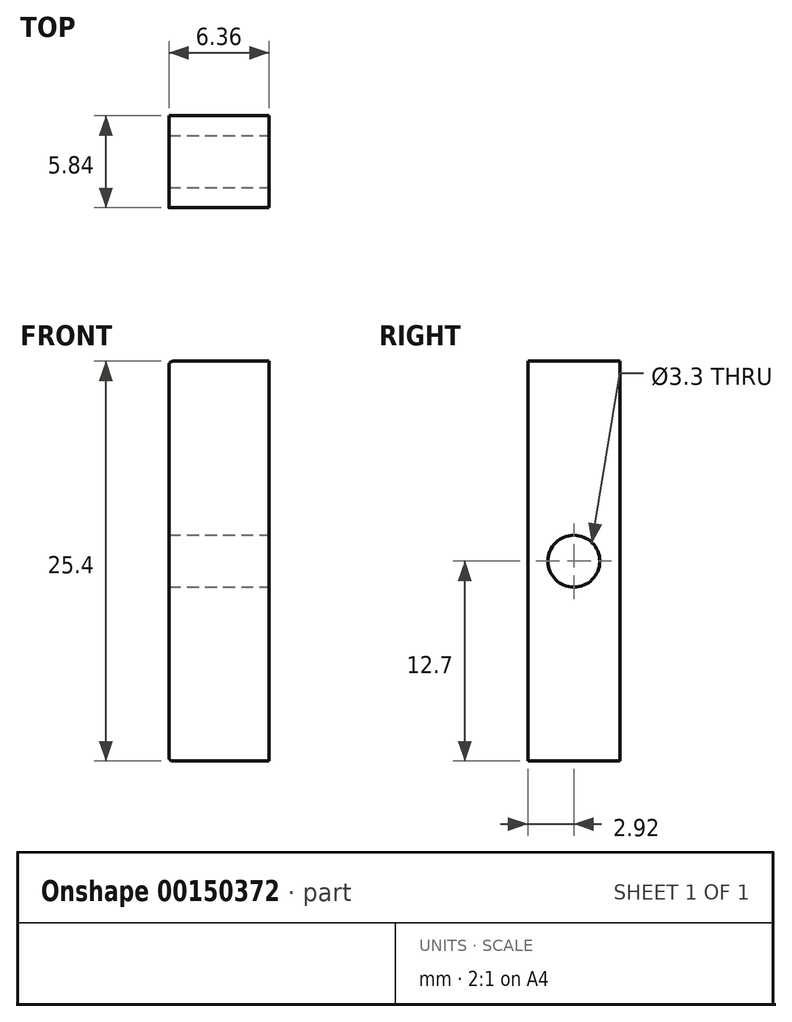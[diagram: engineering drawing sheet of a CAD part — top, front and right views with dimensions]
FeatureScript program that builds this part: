
annotation { "Feature Type Name" : "Feature", "Feature Type Description" : "" }
export const myFeature = defineFeature(function(context is Context, id is Id, definition is map)
    precondition{}
    {
        {
            var Q0;
            Q0=qCreatedBy(makeId("Front.planeOp"),FACE);
            var sketch = newSketch(context, id + "F0", { "sketchPlane" : qUnion([Q0])});
            skLineSegment(sketch, "E0.bottom", {"start": v(4.45, 12.7) * mm, "end": v(-4.45, 12.7) * mm});
            skLineSegment(sketch, "E0.top", {"start": v(4.45, -12.7) * mm, "end": v(-4.45, -12.7) * mm});
            skLineSegment(sketch, "E0.left", {"start": v(4.45, 12.7) * mm, "end": v(4.45, -12.7) * mm});
            skPoint(sketch, "E0.middle", {"position": v(0, 0) * mm});
            skArc(sketch, "E1", {"start": v(-4.45, 11.38) * mm, "mid": v(-3.78, 12.04) * mm, "end": v(-4.45, 12.7) * mm});
            skLineSegment(sketch, "E2", {"start": v(-4.44, 11.38) * mm, "end": v(-4.44, 10.54) * mm});
            skLineSegment(sketch, "E3", {"start": v(-4.45, 12.7) * mm, "end": v(-4.45, 11.38) * mm, "construction": true});
            skArc(sketch, "E4.1.0.0", {"start": v(-4.45, 9.37) * mm, "mid": v(-3.78, 10.03) * mm, "end": v(-4.45, 10.7) * mm});
            skLineSegment(sketch, "E4.1.0.1", {"start": v(-4.45, 9.37) * mm, "end": v(-4.45, 8.53) * mm});
            skArc(sketch, "E4.2.0.0", {"start": v(-4.45, 7.37) * mm, "mid": v(-3.78, 8.03) * mm, "end": v(-4.45, 8.69) * mm});
            skLineSegment(sketch, "E4.2.0.1", {"start": v(-4.45, 7.37) * mm, "end": v(-4.45, 6.53) * mm});
            skArc(sketch, "E4.3.0.0", {"start": v(-4.45, 5.36) * mm, "mid": v(-3.78, 6.02) * mm, "end": v(-4.45, 6.68) * mm});
            skLineSegment(sketch, "E4.3.0.1", {"start": v(-4.45, 5.36) * mm, "end": v(-4.45, 4.52) * mm});
            skArc(sketch, "E4.4.0.0", {"start": v(-4.45, 3.35) * mm, "mid": v(-3.78, 4.01) * mm, "end": v(-4.45, 4.67) * mm});
            skLineSegment(sketch, "E4.4.0.1", {"start": v(-4.45, 3.35) * mm, "end": v(-4.45, 2.51) * mm});
            skArc(sketch, "E4.5.0.0", {"start": v(-4.45, 1.35) * mm, "mid": v(-3.78, 2) * mm, "end": v(-4.45, 2.67) * mm});
            skLineSegment(sketch, "E4.5.0.1", {"start": v(-4.45, 1.35) * mm, "end": v(-4.45, 0.5) * mm});
            skArc(sketch, "E4.6.0.0", {"start": v(-4.45, -0.66) * mm, "mid": v(-3.78, 0) * mm, "end": v(-4.45, 0.66) * mm});
            skLineSegment(sketch, "E4.6.0.1", {"start": v(-4.44, -0.66) * mm, "end": v(-4.44, -1.5) * mm});
            skArc(sketch, "E4.7.0.0", {"start": v(-4.45, -2.67) * mm, "mid": v(-3.78, -2) * mm, "end": v(-4.45, -1.35) * mm});
            skLineSegment(sketch, "E4.7.0.1", {"start": v(-4.44, -2.67) * mm, "end": v(-4.44, -3.5) * mm});
            skArc(sketch, "E4.8.0.0", {"start": v(-4.45, -4.67) * mm, "mid": v(-3.78, -4.01) * mm, "end": v(-4.45, -3.35) * mm});
            skLineSegment(sketch, "E4.8.0.1", {"start": v(-4.44, -4.67) * mm, "end": v(-4.44, -5.51) * mm});
            skArc(sketch, "E4.9.0.0", {"start": v(-4.45, -6.68) * mm, "mid": v(-3.78, -6.02) * mm, "end": v(-4.45, -5.36) * mm});
            skLineSegment(sketch, "E4.9.0.1", {"start": v(-4.44, -6.68) * mm, "end": v(-4.44, -7.52) * mm});
            skArc(sketch, "E4.10.0.0", {"start": v(-4.45, -8.69) * mm, "mid": v(-3.78, -8.03) * mm, "end": v(-4.45, -7.37) * mm});
            skLineSegment(sketch, "E4.10.0.1", {"start": v(-4.44, -8.69) * mm, "end": v(-4.44, -9.53) * mm});
            skArc(sketch, "E4.11.0.0", {"start": v(-4.45, -10.7) * mm, "mid": v(-3.78, -10.03) * mm, "end": v(-4.45, -9.37) * mm});
            skLineSegment(sketch, "E4.11.0.1", {"start": v(-4.44, -10.7) * mm, "end": v(-4.44, -11.53) * mm});
            skArc(sketch, "E4.12.0.0", {"start": v(-4.45, -12.7) * mm, "mid": v(-3.78, -12.04) * mm, "end": v(-4.45, -11.38) * mm});
            skLineSegment(sketch, "E4.direction1", {"start": v(-4.45, 11.38) * mm, "end": v(-4.45, 9.37) * mm, "construction": true});
            skLineSegment(sketch, "E5", {"start": v(-4.45, 12.7) * mm, "end": v(-4.45, -12.7) * mm});
            skSolve(sketch);
        }
        {
            var Q0;
            Q0 = qSketchRegion(id + "F0", true);
            extrude(context, id + "F1", {"entities" : qUnion([Q0]), "endBound" : BoundingType.SYMMETRIC, "depth" : 5.84 * mm});
        }
        {
            var Q0;
            Q0=makeQuery(id+"F1.opExtrude","SWEPT_FACE",FACE,{"disambiguationData":[OSD([sQuery(id+"F0.wireOp",EDGE,"E0.left")])]});
            var sketch = newSketch(context, id + "F2", { "sketchPlane" : qUnion([Q0])});
            skCircle(sketch, "E6", {"center": v(0, 0) * mm, "radius": 1.65 * mm});
            skSolve(sketch);
        }
        {
            var Q0;
            Q0 = qSketchRegion(id + "F2", true);
            extrude(context, id + "F3", {"entities" : qUnion([Q0]), "operationType" : NewBodyOperationType.REMOVE, "oppositeDirection" : true, "depth" : 25.4 * mm});
        }
        {
            var Q0;
            Q0=makeQuery(id+"F1.opExtrude","CAP_FACE",FACE,{"disambiguationData":[OSD([sQuery(id+"F0.wireOp",EDGE,"E0.bottom"),sQuery(id+"F0.wireOp",EDGE,"E0.top"),sQuery(id+"F0.wireOp",EDGE,"E0.left"),sQuery(id+"F0.wireOp",EDGE,"E1"),sQuery(id+"F0.wireOp",EDGE,"E2"),sQuery(id+"F0.wireOp",EDGE,"E4.1.0.0"),sQuery(id+"F0.wireOp",EDGE,"E4.1.0.1"),sQuery(id+"F0.wireOp",EDGE,"E4.2.0.0"),sQuery(id+"F0.wireOp",EDGE,"E4.2.0.1"),sQuery(id+"F0.wireOp",EDGE,"E4.3.0.0"),sQuery(id+"F0.wireOp",EDGE,"E4.3.0.1"),sQuery(id+"F0.wireOp",EDGE,"E4.4.0.0"),sQuery(id+"F0.wireOp",EDGE,"E4.4.0.1"),sQuery(id+"F0.wireOp",EDGE,"E4.5.0.0"),sQuery(id+"F0.wireOp",EDGE,"E4.5.0.1"),sQuery(id+"F0.wireOp",EDGE,"E4.6.0.0"),sQuery(id+"F0.wireOp",EDGE,"E4.6.0.1"),sQuery(id+"F0.wireOp",EDGE,"E4.7.0.0"),sQuery(id+"F0.wireOp",EDGE,"E4.7.0.1"),sQuery(id+"F0.wireOp",EDGE,"E4.8.0.0"),sQuery(id+"F0.wireOp",EDGE,"E4.8.0.1"),sQuery(id+"F0.wireOp",EDGE,"E4.9.0.0"),sQuery(id+"F0.wireOp",EDGE,"E4.9.0.1"),sQuery(id+"F0.wireOp",EDGE,"E4.10.0.0"),sQuery(id+"F0.wireOp",EDGE,"E4.10.0.1"),sQuery(id+"F0.wireOp",EDGE,"E4.11.0.0"),sQuery(id+"F0.wireOp",EDGE,"E4.11.0.1"),sQuery(id+"F0.wireOp",EDGE,"E4.12.0.0")])],"isStart":true});
            var sketch = newSketch(context, id + "F4", { "sketchPlane" : qUnion([Q0])});
            skLineSegment(sketch, "E7.bottom", {"start": v(-1.9, 16.1) * mm, "end": v(-10.5, 16.1) * mm});
            skLineSegment(sketch, "E7.top", {"start": v(-1.9, -16.1) * mm, "end": v(-10.5, -16.1) * mm});
            skLineSegment(sketch, "E7.left", {"start": v(-1.9, 16.1) * mm, "end": v(-1.9, -16.1) * mm});
            skLineSegment(sketch, "E7.right", {"start": v(-10.5, 16.1) * mm, "end": v(-10.5, -16.1) * mm});
            skPoint(sketch, "E7.middle", {"position": v(-6.2, 0) * mm});
            skSolve(sketch);
        }
        {
            var Q0;
            Q0 = qSketchRegion(id + "F4", true);
            extrude(context, id + "F5", {"entities" : qUnion([Q0]), "operationType" : NewBodyOperationType.REMOVE, "oppositeDirection" : true, "depth" : 25.4 * mm});
        }
        {
            var Q0;
            Q0=makeQuery(id+"F1.opExtrude","SWEPT_EDGE",EDGE,{"disambiguationData":[OSD([sQuery(id+"F0.wireOp",EDGE,"E0.bottom"),sQuery(id+"F0.wireOp",EDGE,"E1")])]});
            var Q1;
            Q1=makeQuery(id+"F1.opExtrude","SWEPT_EDGE",EDGE,{"disambiguationData":[OSD([sQuery(id+"F0.wireOp",EDGE,"E0.top"),sQuery(id+"F0.wireOp",EDGE,"E4.12.0.0")])]});
            fillet(context, id + "F6", {"entities" : qUnion([Q0, Q1]), "radius" : 0.25 * mm, "tangentPropagation" : true, "allowEdgeOverflow" : false});
        }
    });
